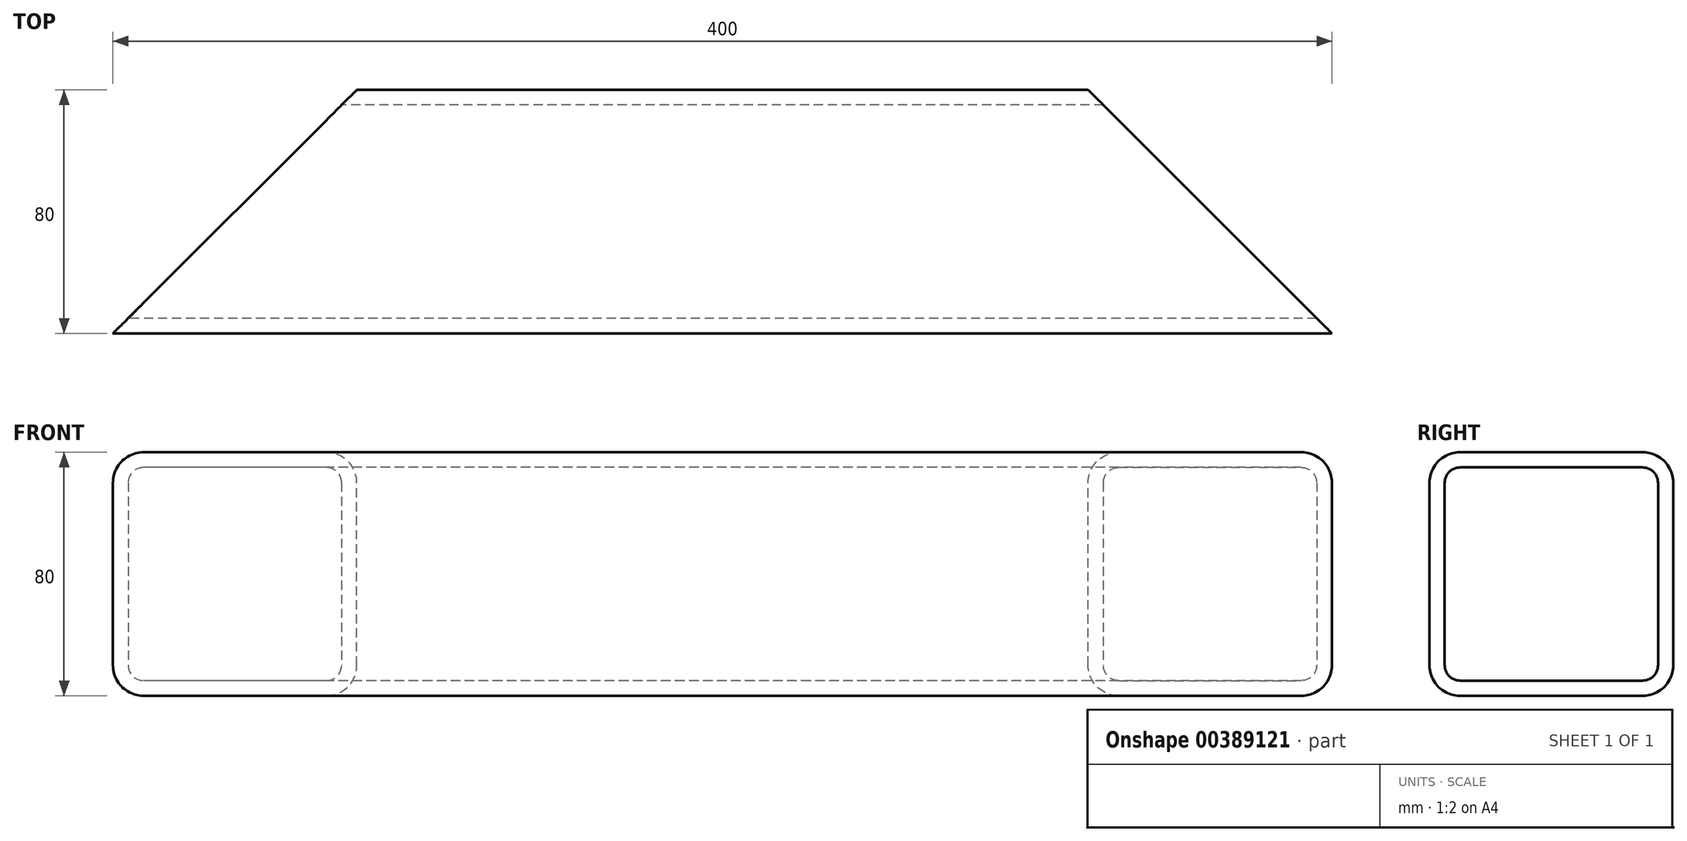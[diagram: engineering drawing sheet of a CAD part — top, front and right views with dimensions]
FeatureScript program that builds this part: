
annotation { "Feature Type Name" : "Feature", "Feature Type Description" : "" }
export const myFeature = defineFeature(function(context is Context, id is Id, definition is map)
    precondition{}
    {
        {
            var Q0;
            Q0=qCreatedBy(makeId("Right.planeOp"),FACE);
            var sketch = newSketch(context, id + "F0", { "sketchPlane" : qUnion([Q0])});
            skLineSegment(sketch, "E0.bottom", {"start": v(30, 40) * mm, "end": v(-30, 40) * mm});
            skLineSegment(sketch, "E0.top", {"start": v(30, -40) * mm, "end": v(-30, -40) * mm});
            skLineSegment(sketch, "E0.left", {"start": v(40, 30) * mm, "end": v(40, -30) * mm});
            skLineSegment(sketch, "E0.right", {"start": v(-40, 30) * mm, "end": v(-40, -30) * mm});
            skPoint(sketch, "E0.middle", {"position": v(0, 0) * mm});
            skPoint(sketch, "E1.visualSharp", {"position": v(-40, 40) * mm});
            skArc(sketch, "E1.filletArc", {"start": v(-30, 40) * mm, "mid": v(-37.07, 37.07) * mm, "end": v(-40, 30) * mm});
            skPoint(sketch, "E2.visualSharp", {"position": v(40, 40) * mm});
            skArc(sketch, "E2.filletArc", {"start": v(40, 30) * mm, "mid": v(37.07, 37.07) * mm, "end": v(30, 40) * mm});
            skPoint(sketch, "E3.visualSharp", {"position": v(40, -40) * mm});
            skArc(sketch, "E3.filletArc", {"start": v(30, -40) * mm, "mid": v(37.07, -37.07) * mm, "end": v(40, -30) * mm});
            skPoint(sketch, "E4.visualSharp", {"position": v(-40, -40) * mm});
            skArc(sketch, "E4.filletArc", {"start": v(-40, -30) * mm, "mid": v(-37.07, -37.07) * mm, "end": v(-30, -40) * mm});
            skArc(sketch, "E5.0", {"start": v(35, 30) * mm, "mid": v(33.54, 33.54) * mm, "end": v(30, 35) * mm});
            skLineSegment(sketch, "E5.1", {"start": v(35, 30) * mm, "end": v(35, -30) * mm});
            skLineSegment(sketch, "E5.2", {"start": v(30, 35) * mm, "end": v(-30, 35) * mm});
            skArc(sketch, "E5.3", {"start": v(30, -35) * mm, "mid": v(33.54, -33.54) * mm, "end": v(35, -30) * mm});
            skArc(sketch, "E5.4", {"start": v(-30, 35) * mm, "mid": v(-33.54, 33.54) * mm, "end": v(-35, 30) * mm});
            skLineSegment(sketch, "E5.5", {"start": v(-35, 30) * mm, "end": v(-35, -30) * mm});
            skArc(sketch, "E5.6", {"start": v(-35, -30) * mm, "mid": v(-33.54, -33.54) * mm, "end": v(-30, -35) * mm});
            skLineSegment(sketch, "E5.7", {"start": v(30, -35) * mm, "end": v(-30, -35) * mm});
            skSolve(sketch);
        }
        {
            var Q0;
            Q0=qSketchRegion(id+"F0",true);
            extrude(context, id + "F1", {"entities" : qUnion([Q0]), "endBound" : BoundingType.SYMMETRIC, "depth" : 400 * mm});
        }
        {
            var Q0;
            Q0=makeQuery(id+"F1.opExtrude","SWEPT_FACE",FACE,{"disambiguationData":[OSD([sQuery(id+"F0.wireOp",EDGE,"E0.bottom")])]});
            var sketch = newSketch(context, id + "F2", { "sketchPlane" : qUnion([Q0])});
            skLineSegment(sketch, "E6", {"start": v(-200, -40) * mm, "end": v(-120, 40) * mm});
            skLineSegment(sketch, "E7", {"start": v(-120, 40) * mm, "end": v(-200, 40) * mm});
            skLineSegment(sketch, "E8", {"start": v(-200, 40) * mm, "end": v(-200, -40) * mm});
            skLineSegment(sketch, "E9", {"start": v(0, 30) * mm, "end": v(0, -30) * mm, "construction": true});
            skLineSegment(sketch, "E10.MirrorCS", {"start": v(200, 40) * mm, "end": v(200, -40) * mm});
            skLineSegment(sketch, "E11.MirrorCS", {"start": v(200, -40) * mm, "end": v(120, 40) * mm});
            skLineSegment(sketch, "E12.MirrorCS", {"start": v(120, 40) * mm, "end": v(200, 40) * mm});
            skSolve(sketch);
        }
        {
            var Q0;
            Q0=qSketchRegion(id+"F2",true);
            extrude(context, id + "F3", {"entities" : qUnion([Q0]), "operationType" : NewBodyOperationType.REMOVE, "endBound" : BoundingType.THROUGH_ALL, "oppositeDirection" : true, "depth" : 25 * mm});
        }
    });
